# Revit family: FA_БетонноеОснованиеДляМачты_58002_EZETEK
name_source: partatom
category: Системы пожарной сигнализации
revit_build: Autodesk Revit 2017 (Build: 20170118_1100(x64)
units: mm (PartAtom-declared; Revit-internal decimal feet)

## family parameters
Всегда вертикально = Да
На основе рабочей плоскости = Нет
Общий = Да
При загрузке вырезать с полостями = Нет
Размер круглого соединителя = Использовать радиус
Сохранять ориентацию аннотаций = Нет
Тип детали = Нормальный
Точка расчета площади = Нет

## types (1)
- БетонноеОснованиеДляМачты_58002
    ADSK_Версия Revit = 2017
    ADSK_Единица измерения = шт.
    ADSK_Завод-изготовитель = Ezetek
    ADSK_Код изделия = 58002
    ADSK_Количество = 1
    ADSK_Марка = 58002
    ADSK_Масса = 35.5
    ADSK_Масса_Текст = 35.50
    ADSK_Материал = BIMLIB_Бетон_EZETEK
    ADSK_Наименование = Бетонное основание для мачты СММ
    ADSK_Обозначение = 58002
    URL = https://ezetek.ru
    Группа модели = Молниеотводы и мачты на утяжелителях
    Изготовитель = Ezetek
    Описание = Бетонное основание позволяет установить на плоской
кровле молниеприемную мачту диаметром 32 мм
и общей высотой до 4 метров. Для фиксации мачты
на основании служит труба внешним диаметром
40 мм. Бетонное основание также применяется для
выполнения молниезащиты отдельных выступающих
на кровле объектов: вентиляционных шахт, элементов
системы кондиционирования и т. д. Для подключения
токоотвода в комплектацию бетонного основания
включен один зажим под пруток диаметром 8-10 мм —
Арт. 91092 Держатель проводника круглого.
    Угол = 90.00°
